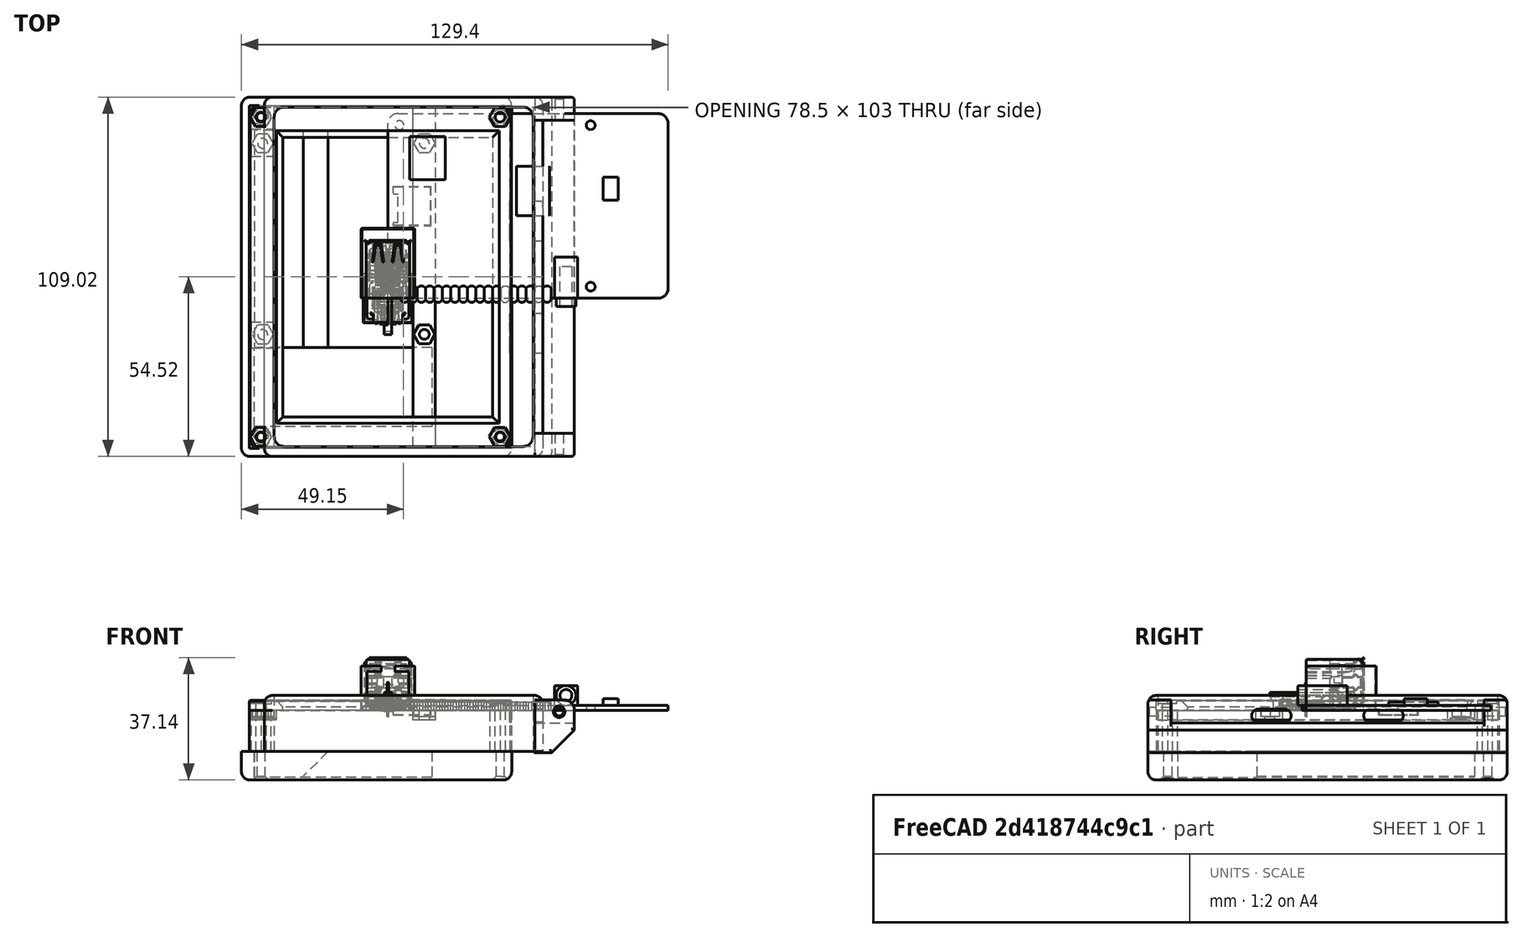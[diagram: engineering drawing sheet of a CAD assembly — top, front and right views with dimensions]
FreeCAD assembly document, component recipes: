
FREECAD ASSEMBLY — COMPONENT RECIPES ("computer-side")

This assembly document has 5 components, labeled P0..P4 below (a component is one placed body or linked part). 4 of them carry a construction recipe — the FreeCAD feature program that regenerates the part from scratch, quoted from this document or its linked companion documents; the rest are supplied as boundary geometry only. No exploded tour is included for this assembly.
COMPONENT P0 — recipe-attached ("epaper module tray", modeled in this document).
Construction recipe (the document's own serialized feature program — sketch geometry with constraints, then the solid features built on it; lengths are millimeters unless a unit is written):

FEATURE [Sketcher::SketchObject] Sketch002
  FullyConstrained = false
  MapMode = 5
  Support = -> [XY_Plane005]
  sketch-geometry (16):
    g0: LineSegment StartX=34 StartY=-45 StartZ=0 EndX=-38.5 EndY=-45 EndZ=0
    g1: LineSegment StartX=-41.5 StartY=-42 StartZ=0 EndX=-41.5 EndY=55 EndZ=0
    g2: LineSegment StartX=-38.5 StartY=58 StartZ=0 EndX=34 EndY=58 EndZ=0
    g3: LineSegment StartX=37 StartY=55 StartZ=0 EndX=37 EndY=-42 EndZ=0
    g4: LineSegment StartX=-42 StartY=58.5 StartZ=0 EndX=37.5 EndY=58.5 EndZ=0
    g5: LineSegment StartX=37.5 StartY=58.5 StartZ=0 EndX=37.5 EndY=-45.5 EndZ=0
    g6: LineSegment StartX=37.5 StartY=-45.5 StartZ=0 EndX=-42 EndY=-45.5 EndZ=0
    g7: LineSegment StartX=-42 StartY=-45.5 StartZ=0 EndX=-42 EndY=58.5 EndZ=0
    g8: Circle CenterX=-38.5 CenterY=55 CenterZ=0 NormalX=0 NormalY=0 NormalZ=1 AngleXU=0 Radius=1.5
    g9: Circle CenterX=34 CenterY=55 CenterZ=0 NormalX=0 NormalY=0 NormalZ=1 AngleXU=0 Radius=1.5
    g10: Circle CenterX=-38.5 CenterY=-42 CenterZ=0 NormalX=0 NormalY=0 NormalZ=1 AngleXU=0 Radius=1.5
    g11: Circle CenterX=34 CenterY=-42 CenterZ=0 NormalX=0 NormalY=0 NormalZ=1 AngleXU=0 Radius=1.5
    g12: ArcOfCircle CenterX=-38.5 CenterY=55 CenterZ=0 NormalX=0 NormalY=0 NormalZ=1 AngleXU=0 Radius=3 StartAngle=3.14159 EndAngle=7.85398
    g13: ArcOfCircle CenterX=34 CenterY=55 CenterZ=0 NormalX=0 NormalY=0 NormalZ=1 AngleXU=0 Radius=3 StartAngle=1.5708 EndAngle=6.28319
    g14: ArcOfCircle CenterX=34 CenterY=-42 CenterZ=0 NormalX=0 NormalY=0 NormalZ=1 AngleXU=0 Radius=3 StartAngle=0 EndAngle=4.71239
    g15: ArcOfCircle CenterX=-38.5 CenterY=-42 CenterZ=0 NormalX=0 NormalY=0 NormalZ=1 AngleXU=0 Radius=3 StartAngle=4.71239 EndAngle=9.42478
  constraints (32):
    c: Horizontal(g0)
    c: Horizontal(g2)
    c: Vertical(g1)
    c: Vertical(g3)
    c: Coincident(g4,g5)
    c: Coincident(g5,g6)
    c: Coincident(g6,g7)
    c: Coincident(g7,g4)
    c: Horizontal(g4)
    c: Horizontal(g6)
    c: Vertical(g5)
    c: Vertical(g7)
    c: Equal(g10,g11)
    c: Equal(g10,g8)
    c: Equal(g10,g9)
    c: Diameter(g10) = 3
    c: Coincident(g12,g8)
    c: Coincident(g13,g9)
    c: Coincident(g14,g11)
    c: Coincident(g15,g10)
    c: Equal(g12,g13)
    c: Equal(g12,g14)
    c: Equal(g12,g15)
    c: Diameter(g12) = 6
    c: Coincident(g13,g3)
    c: Coincident(g13,g2)
    c: Coincident(g12,g2)
    c: Coincident(g12,g1)
    c: Coincident(g1,g15)
    c: Coincident(g0,g15)
    c: Coincident(g14,g0)
    c: Coincident(g14,g3)
FEATURE [PartDesign::Pad] Pad002
  Direction = (0,0,1)
  Length = 12.5
  Length2 = 10
  Profile = -> Sketch002
  ReferenceAxis = -> Sketch002 [N_Axis]
  Reversed = true
  Type = 0
FEATURE [Sketcher::SketchObject] Sketch
  FullyConstrained = false
  MapMode = 5
  Support = -> [XY_Plane005]
  sketch-geometry (5):
    g0: LineSegment StartX=-33.867 StartY=51.1954 StartZ=0 EndX=-33.867 EndY=42.9605 EndZ=0
    g1: LineSegment StartX=-33.867 StartY=51.1954 StartZ=0 EndX=-41.8883 EndY=51.1954 EndZ=0
    g2: LineSegment StartX=-33.867 StartY=42.9605 StartZ=0 EndX=-41.8883 EndY=42.9605 EndZ=0
    g3: LineSegment StartX=-41.8883 StartY=51.1954 StartZ=0 EndX=-41.8883 EndY=42.9605 EndZ=0
    g4: Circle CenterX=-37.9976 CenterY=47.0105 CenterZ=0 NormalX=0 NormalY=0 NormalZ=1 AngleXU=0 Radius=1.5
  constraints (9):
    c: Vertical(g0)
    c: Coincident(g1,g0)
    c: Horizontal(g1)
    c: Coincident(g2,g0)
    c: Horizontal(g2)
    c: Coincident(g3,g1)
    c: Vertical(g3)
    c: Coincident(g3,g2)
    c: Diameter(g4) = 3
FEATURE [PartDesign::Pad] Pad
  BaseFeature = -> Pad002
  Direction = (0,0,1)
  Length = 2.5
  Length2 = 10
  Profile = -> Sketch
  ReferenceAxis = -> Sketch [N_Axis]
  Reversed = true
  Type = 0
FEATURE [Sketcher::SketchObject] Sketch032
  FullyConstrained = false
  MapMode = 5
  Support = -> [Pad]
  sketch-geometry (7):
    g0: LineSegment StartX=-34.726 StartY=46.9826 StartZ=0 EndX=-36.351 EndY=49.7971 EndZ=0
    g1: LineSegment StartX=-36.351 StartY=49.7971 StartZ=0 EndX=-39.601 EndY=49.7971 EndZ=0
    g2: LineSegment StartX=-39.601 StartY=49.7971 StartZ=0 EndX=-41.226 EndY=46.9826 EndZ=0
    g3: LineSegment StartX=-41.226 StartY=46.9826 StartZ=0 EndX=-39.601 EndY=44.168 EndZ=0
    g4: LineSegment StartX=-39.601 StartY=44.168 StartZ=0 EndX=-36.351 EndY=44.168 EndZ=0
    g5: LineSegment StartX=-36.351 StartY=44.168 StartZ=0 EndX=-34.726 EndY=46.9826 EndZ=0
    g6: Circle CenterX=-37.976 CenterY=46.9826 CenterZ=0 NormalX=0 NormalY=0 NormalZ=1 AngleXU=0 Radius=3.25
  constraints (15):
    c: Coincident(g0,g1)
    c: Coincident(g1,g2)
    c: Coincident(g2,g3)
    c: Coincident(g3,g4)
    c: Coincident(g4,g5)
    c: Coincident(g5,g0)
    c: Equal(g0, g1-g5) x5
    c: PointOnObject(g0,g6)
    c: PointOnObject(g1,g6)
    c: PointOnObject(g2,g6)
    c: PointOnObject(g3,g6)
    c: PointOnObject(g4,g6)
    c: PointOnObject(g5,g6)
    c: Diameter(g6) = 6.5
    c: Horizontal(g1)
FEATURE [PartDesign::Pocket] Pocket
  BaseFeature = -> Pad
  Direction = (0,0,-1)
  Length = 2
  Length2 = 5
  Profile = -> Sketch032
  ReferenceAxis = -> Sketch032 [N_Axis]
  Type = 0
FEATURE [Sketcher::SketchObject] Sketch033
  FullyConstrained = false
  MapMode = 5
  Support = -> [XY_Plane005]
  sketch-geometry (5):
    g0: LineSegment StartX=-41.8965 StartY=-7.25864 StartZ=0 EndX=-33.9497 EndY=-7.25864 EndZ=0
    g1: LineSegment StartX=-33.9497 StartY=-7.25864 StartZ=0 EndX=-33.9497 EndY=-15.2055 EndZ=0
    g2: LineSegment StartX=-33.9497 StartY=-15.2055 StartZ=0 EndX=-41.8965 EndY=-15.2055 EndZ=0
    g3: LineSegment StartX=-41.8965 StartY=-15.2055 StartZ=0 EndX=-41.8965 EndY=-7.25864 EndZ=0
    g4: Circle CenterX=-37.9911 CenterY=-11.0086 CenterZ=0 NormalX=0 NormalY=0 NormalZ=1 AngleXU=0 Radius=1.5
  constraints (9):
    c: Coincident(g0,g1)
    c: Coincident(g1,g2)
    c: Coincident(g2,g3)
    c: Coincident(g3,g0)
    c: Horizontal(g0)
    c: Horizontal(g2)
    c: Vertical(g1)
    c: Vertical(g3)
    c: Diameter(g4) = 3
FEATURE [PartDesign::Pad] Pad003
  BaseFeature = -> Pocket
  Direction = (0,0,1)
  Length = 3
  Length2 = 10
  Profile = -> Sketch033
  ReferenceAxis = -> Sketch033 [N_Axis]
  Reversed = true
  Type = 0
FEATURE [Sketcher::SketchObject] Sketch034
  FullyConstrained = false
  MapMode = 5
  Support = -> [XY_Plane005]
  sketch-geometry (6):
    g0: LineSegment StartX=7.58059 StartY=58.3477 StartZ=0 EndX=14.382 EndY=58.3477 EndZ=0
    g1: LineSegment StartX=14.382 StartY=58.3477 StartZ=0 EndX=14.382 EndY=-45.3233 EndZ=0
    g2: LineSegment StartX=14.382 StartY=-45.3233 StartZ=0 EndX=7.58059 EndY=-45.3233 EndZ=0
    g3: LineSegment StartX=7.58059 StartY=-45.3233 StartZ=0 EndX=7.58059 EndY=58.3477 EndZ=0
    g4: Circle CenterX=11.0339 CenterY=47.0265 CenterZ=0 NormalX=0 NormalY=0 NormalZ=1 AngleXU=0 Radius=1.5
    g5: Circle CenterX=11.0339 CenterY=-10.9673 CenterZ=0 NormalX=0 NormalY=0 NormalZ=1 AngleXU=0 Radius=1.5
  constraints (11):
    c: Coincident(g0,g1)
    c: Coincident(g1,g2)
    c: Coincident(g2,g3)
    c: Coincident(g3,g0)
    c: Horizontal(g0)
    c: Horizontal(g2)
    c: Vertical(g1)
    c: Vertical(g3)
    c: Equal(g5,g4)
    c: Diameter(g5) = 3
    c: Vertical(g4,g5)
FEATURE [PartDesign::Pad] Pad004
  BaseFeature = -> Pad003
  Direction = (0,0,1)
  Length = 3
  Length2 = 10
  Profile = -> Sketch034
  ReferenceAxis = -> Sketch034 [N_Axis]
  Reversed = true
  Type = 0
FEATURE [Sketcher::SketchObject] Sketch035
  FullyConstrained = false
  MapMode = 5
  Support = -> [Pad004]
  sketch-geometry (7):
    g0: LineSegment StartX=-36.3268 StartY=-8.14599 StartZ=0 EndX=-39.5768 EndY=-8.14599 EndZ=0
    g1: LineSegment StartX=-39.5768 StartY=-8.14599 StartZ=0 EndX=-41.2018 EndY=-10.9606 EndZ=0
    g2: LineSegment StartX=-41.2018 StartY=-10.9606 StartZ=0 EndX=-39.5768 EndY=-13.7752 EndZ=0
    g3: LineSegment StartX=-39.5768 StartY=-13.7752 StartZ=0 EndX=-36.3268 EndY=-13.7752 EndZ=0
    g4: LineSegment StartX=-36.3268 StartY=-13.7752 StartZ=0 EndX=-34.7018 EndY=-10.9606 EndZ=0
    g5: LineSegment StartX=-34.7018 StartY=-10.9606 StartZ=0 EndX=-36.3268 EndY=-8.14599 EndZ=0
    g6: Circle CenterX=-37.9518 CenterY=-10.9606 CenterZ=0 NormalX=0 NormalY=0 NormalZ=1 AngleXU=0 Radius=3.25
  constraints (15):
    c: Coincident(g0,g1)
    c: Coincident(g1,g2)
    c: Coincident(g2,g3)
    c: Coincident(g3,g4)
    c: Coincident(g4,g5)
    c: Coincident(g5,g0)
    c: Equal(g0, g1-g5) x5
    c: PointOnObject(g0,g6)
    c: PointOnObject(g1,g6)
    c: PointOnObject(g2,g6)
    c: PointOnObject(g3,g6)
    c: PointOnObject(g4,g6)
    c: PointOnObject(g5,g6)
    c: Horizontal(g0)
    c: Diameter(g6) = 6.5
FEATURE [PartDesign::Pocket] Pocket001
  BaseFeature = -> Pad004
  Direction = (0,0,-1)
  Length = 2
  Length2 = 5
  Profile = -> Sketch035
  ReferenceAxis = -> Sketch035 [N_Axis]
  Type = 0
FEATURE [Sketcher::SketchObject] Sketch036
  FullyConstrained = false
  MapMode = 5
  Support = -> [Pocket001]
  sketch-geometry (7):
    g0: LineSegment StartX=12.6781 StartY=49.8538 StartZ=0 EndX=9.42807 EndY=49.8538 EndZ=0
    g1: LineSegment StartX=9.42807 StartY=49.8538 StartZ=0 EndX=7.80307 EndY=47.0392 EndZ=0
    g2: LineSegment StartX=7.80307 StartY=47.0392 StartZ=0 EndX=9.42807 EndY=44.2246 EndZ=0
    g3: LineSegment StartX=9.42807 StartY=44.2246 StartZ=0 EndX=12.6781 EndY=44.2246 EndZ=0
    g4: LineSegment StartX=12.6781 StartY=44.2246 StartZ=0 EndX=14.3031 EndY=47.0392 EndZ=0
    g5: LineSegment StartX=14.3031 StartY=47.0392 StartZ=0 EndX=12.6781 EndY=49.8538 EndZ=0
    g6: Circle CenterX=11.0531 CenterY=47.0392 CenterZ=0 NormalX=0 NormalY=0 NormalZ=1 AngleXU=0 Radius=3.25
  constraints (15):
    c: Coincident(g0,g1)
    c: Coincident(g1,g2)
    c: Coincident(g2,g3)
    c: Coincident(g3,g4)
    c: Coincident(g4,g5)
    c: Coincident(g5,g0)
    c: Equal(g0, g1-g5) x5
    c: PointOnObject(g0,g6)
    c: PointOnObject(g1,g6)
    c: PointOnObject(g2,g6)
    c: PointOnObject(g3,g6)
    c: PointOnObject(g4,g6)
    c: PointOnObject(g5,g6)
    c: Diameter(g6) = 6.5
    c: Horizontal(g0)
FEATURE [PartDesign::Pocket] Pocket002
  BaseFeature = -> Pocket001
  Direction = (0,0,-1)
  Length = 2
  Length2 = 5
  Profile = -> Sketch036
  ReferenceAxis = -> Sketch036 [N_Axis]
  Type = 0
FEATURE [Sketcher::SketchObject] Sketch037
  FullyConstrained = false
  MapMode = 5
  Support = -> [Pocket002]
  sketch-geometry (7):
    g0: LineSegment StartX=12.6362 StartY=-8.1216 StartZ=0 EndX=9.3862 EndY=-8.1216 EndZ=0
    g1: LineSegment StartX=9.3862 StartY=-8.1216 StartZ=0 EndX=7.7612 EndY=-10.9362 EndZ=0
    g2: LineSegment StartX=7.7612 StartY=-10.9362 StartZ=0 EndX=9.3862 EndY=-13.7508 EndZ=0
    g3: LineSegment StartX=9.3862 StartY=-13.7508 StartZ=0 EndX=12.6362 EndY=-13.7508 EndZ=0
    g4: LineSegment StartX=12.6362 StartY=-13.7508 StartZ=0 EndX=14.2612 EndY=-10.9362 EndZ=0
    g5: LineSegment StartX=14.2612 StartY=-10.9362 StartZ=0 EndX=12.6362 EndY=-8.1216 EndZ=0
    g6: Circle CenterX=11.0112 CenterY=-10.9362 CenterZ=0 NormalX=0 NormalY=0 NormalZ=1 AngleXU=0 Radius=3.25
  constraints (15):
    c: Coincident(g0,g1)
    c: Coincident(g1,g2)
    c: Coincident(g2,g3)
    c: Coincident(g3,g4)
    c: Coincident(g4,g5)
    c: Coincident(g5,g0)
    c: Equal(g0, g1-g5) x5
    c: PointOnObject(g0,g6)
    c: PointOnObject(g1,g6)
    c: PointOnObject(g2,g6)
    c: PointOnObject(g3,g6)
    c: PointOnObject(g4,g6)
    c: PointOnObject(g5,g6)
    c: Diameter(g6) = 6.5
    c: Horizontal(g0)
FEATURE [PartDesign::Pocket] Pocket003
  BaseFeature = -> Pocket002
  Direction = (0,0,-1)
  Length = 2
  Length2 = 5
  Profile = -> Sketch037
  ReferenceAxis = -> Sketch037 [N_Axis]
  Type = 0
FEATURE [Sketcher::SketchObject] Sketch058
  AttachmentOffset = pos=(0,0,37) rot=(0,0,1;0rad)
  FullyConstrained = false
  MapMode = 5
  Placement = pos=(37,-8.2e-15,8.2e-15) rot=(0.57735,0.57735,0.57735;2.0944rad)
  Support = -> [YZ_Plane005]
  sketch-geometry (8):
    g0: ArcOfCircle CenterX=-14.544 CenterY=-1.63349 CenterZ=0 NormalX=0 NormalY=0 NormalZ=1 AngleXU=0 Radius=2 StartAngle=1.5708 EndAngle=4.71239
    g1: ArcOfCircle CenterX=-6.544 CenterY=-1.63349 CenterZ=0 NormalX=0 NormalY=0 NormalZ=1 AngleXU=0 Radius=2 StartAngle=4.71239 EndAngle=7.85398
    g2: LineSegment StartX=-14.544 StartY=-3.63349 StartZ=0 EndX=-6.54401 EndY=-3.63349 EndZ=0
    g3: LineSegment StartX=-6.54401 StartY=0.366508 StartZ=0 EndX=-14.544 EndY=0.366508 EndZ=0
    g4: ArcOfCircle CenterX=19.456 CenterY=-1.63349 CenterZ=0 NormalX=0 NormalY=0 NormalZ=1 AngleXU=0 Radius=2 StartAngle=1.5708 EndAngle=4.71239
    g5: ArcOfCircle CenterX=27.456 CenterY=-1.63349 CenterZ=0 NormalX=0 NormalY=0 NormalZ=1 AngleXU=0 Radius=2 StartAngle=4.71239 EndAngle=7.85398
    g6: LineSegment StartX=19.456 StartY=-3.63349 StartZ=0 EndX=27.456 EndY=-3.63349 EndZ=0
    g7: LineSegment StartX=27.456 StartY=0.366508 StartZ=0 EndX=19.456 EndY=0.366508 EndZ=0
  constraints (18):
    c: Tangent(g0,g2) = -1.5708
    c: Tangent(g2,g1) = -1.5708
    c: Tangent(g1,g3) = -1.5708
    c: Tangent(g3,g0) = -1.5708
    c: Equal(g0,g1)
    c: Tangent(g4,g6) = -1.5708
    c: Tangent(g6,g5) = -1.5708
    c: Tangent(g5,g7) = -1.5708
    c: Tangent(g7,g4) = -1.5708
    c: Equal(g4,g5)
    c: Horizontal(g3)
    c: Horizontal(g7)
    c: Equal(g3,g7)
    c: Equal(g1,g4)
    c: DistanceX(g1,g4) = 26
    c: DistanceY(g0,g0) = 4
    c: Horizontal(g1,g4)
    c: DistanceX(g0,g1) = 8
FEATURE [PartDesign::Pocket] Pocket027
  BaseFeature = -> Pocket003
  Direction = (-1,2e-16,-3e-16)
  Length = 0
  Length2 = 5
  Profile = -> Sketch058
  ReferenceAxis = -> Sketch058 [N_Axis]
  Reversed = true
  Type = 2
FEATURE [PartDesign::Body] Body002
  Group = -> [Sketch002,Pad002,Sketch,Pad,Sketch032,Pocket,Sketch033,Pad003,Sketch034,Pad004,Sketch035,Pocket001,Sketch036,Pocket002,Sketch037,Pocket003,Sketch058,Pocket027]
  Origin = -> Origin005
  Tip = -> Pocket027
COMPONENT P1 — recipe-attached ("epaper module cover", modeled in this document).
Construction recipe (the document's own serialized feature program — sketch geometry with constraints, then the solid features built on it; lengths are millimeters unless a unit is written):

FEATURE [PartDesign::Body] Body003  label="nuts"
  Origin = -> Origin007
FEATURE [Sketcher::SketchObject] Sketch003
  AttachmentOffset = pos=(0,0,2) rot=(0,0,1;0rad)
  FullyConstrained = false
  MapMode = 5
  Placement = pos=(0,0,2) rot=(0,0,1;0rad)
  Support = -> [XY_Plane008]
  sketch-geometry (7):
    g0: LineSegment StartX=-35.284 StartY=54.9433 StartZ=0 EndX=-36.909 EndY=57.7579 EndZ=0
    g1: LineSegment StartX=-36.909 StartY=57.7579 StartZ=0 EndX=-40.159 EndY=57.7579 EndZ=0
    g2: LineSegment StartX=-40.159 StartY=57.7579 StartZ=0 EndX=-41.784 EndY=54.9433 EndZ=0
    g3: LineSegment StartX=-41.784 StartY=54.9433 StartZ=0 EndX=-40.159 EndY=52.1287 EndZ=0
    g4: LineSegment StartX=-40.159 StartY=52.1287 StartZ=0 EndX=-36.909 EndY=52.1287 EndZ=0
    g5: LineSegment StartX=-36.909 StartY=52.1287 StartZ=0 EndX=-35.284 EndY=54.9433 EndZ=0
    g6: Circle CenterX=-38.534 CenterY=54.9433 CenterZ=0 NormalX=0 NormalY=0 NormalZ=1 AngleXU=0 Radius=3.25
  constraints (14):
    c: Coincident(g0,g1)
    c: Coincident(g1,g2)
    c: Coincident(g2,g3)
    c: Coincident(g3,g4)
    c: Coincident(g4,g5)
    c: Coincident(g5,g0)
    c: Equal(g0, g1-g5) x5
    c: PointOnObject(g0,g6)
    c: PointOnObject(g1,g6)
    c: PointOnObject(g2,g6)
    c: PointOnObject(g3,g6)
    c: PointOnObject(g4,g6)
    c: PointOnObject(g5,g6)
    c: Horizontal(g1)
FEATURE [Sketcher::SketchObject] Sketch005
  FullyConstrained = false
  MapMode = 5
  Support = -> [XY_Plane008]
  sketch-geometry (8):
    g0: LineSegment StartX=-42 StartY=58.5 StartZ=0 EndX=37.5 EndY=58.5 EndZ=0
    g1: LineSegment StartX=37.5 StartY=58.5 StartZ=0 EndX=37.5 EndY=-45.5 EndZ=0
    g2: LineSegment StartX=37.5 StartY=-45.5 StartZ=0 EndX=-42 EndY=-45.5 EndZ=0
    g3: LineSegment StartX=-42 StartY=-45.5 StartZ=0 EndX=-42 EndY=58.5 EndZ=0
    g4: LineSegment StartX=-31.8439 StartY=48.8107 StartZ=0 EndX=31.7561 EndY=48.8107 EndZ=0
    g5: LineSegment StartX=31.7561 StartY=48.8107 StartZ=0 EndX=31.7561 EndY=-35.9893 EndZ=0
    g6: LineSegment StartX=31.7561 StartY=-35.9893 StartZ=0 EndX=-31.8439 EndY=-35.9893 EndZ=0
    g7: LineSegment StartX=-31.8439 StartY=-35.9893 StartZ=0 EndX=-31.8439 EndY=48.8107 EndZ=0
  constraints (22):
    c: Coincident(g0,g1)
    c: Coincident(g1,g2)
    c: Coincident(g2,g3)
    c: Coincident(g3,g0)
    c: Horizontal(g0)
    c: Horizontal(g2)
    c: Vertical(g1)
    c: Vertical(g3)
    c: Coincident(g4,g5)
    c: Coincident(g5,g6)
    c: Coincident(g6,g7)
    c: Coincident(g7,g4)
    c: Horizontal(g4)
    c: Horizontal(g6)
    c: Vertical(g5)
    c: Vertical(g7)
    c: DistanceX(g4,g4) = 63.6
    c: DistanceY(g7,g7) = 84.8
    c: DistanceX(g0,g0) = 79.5
    c: DistanceY(g3,g3) = 104
    c: DistanceY(g1,g-1) = 45.5
    c: DistanceX(g-1,g1) = 37.5
FEATURE [PartDesign::Pad] Pad005
  Direction = (0,0,1)
  Length = 3
  Length2 = 10
  Profile = -> Sketch005
  ReferenceAxis = -> Sketch005 [N_Axis]
  Type = 0
FEATURE [PartDesign::Pocket] Pocket004
  BaseFeature = -> Pad005
  Direction = (0,0,-1)
  Length = 2
  Length2 = 5
  Profile = -> Sketch003
  ReferenceAxis = -> Sketch003 [N_Axis]
  Reversed = true
  Type = 0
FEATURE [Sketcher::SketchObject] Sketch006
  AttachmentOffset = pos=(0,0,2) rot=(0,0,1;0rad)
  FullyConstrained = false
  MapMode = 5
  Placement = pos=(0,0,2) rot=(0,0,1;0rad)
  Support = -> [XY_Plane008]
  sketch-geometry (7):
    g0: LineSegment StartX=-35.284 StartY=-42.0567 StartZ=0 EndX=-36.909 EndY=-39.2421 EndZ=0
    g1: LineSegment StartX=-36.909 StartY=-39.2421 StartZ=0 EndX=-40.159 EndY=-39.2421 EndZ=0
    g2: LineSegment StartX=-40.159 StartY=-39.2421 StartZ=0 EndX=-41.784 EndY=-42.0567 EndZ=0
    g3: LineSegment StartX=-41.784 StartY=-42.0567 StartZ=0 EndX=-40.159 EndY=-44.8713 EndZ=0
    g4: LineSegment StartX=-40.159 StartY=-44.8713 StartZ=0 EndX=-36.909 EndY=-44.8713 EndZ=0
    g5: LineSegment StartX=-36.909 StartY=-44.8713 StartZ=0 EndX=-35.284 EndY=-42.0567 EndZ=0
    g6: Circle CenterX=-38.534 CenterY=-42.0567 CenterZ=0 NormalX=0 NormalY=0 NormalZ=1 AngleXU=0 Radius=3.25
  constraints (14):
    c: Coincident(g0,g1)
    c: Coincident(g1,g2)
    c: Coincident(g2,g3)
    c: Coincident(g3,g4)
    c: Coincident(g4,g5)
    c: Coincident(g5,g0)
    c: Equal(g0, g1-g5) x5
    c: PointOnObject(g0,g6)
    c: PointOnObject(g1,g6)
    c: PointOnObject(g2,g6)
    c: PointOnObject(g3,g6)
    c: PointOnObject(g4,g6)
    c: PointOnObject(g5,g6)
    c: Horizontal(g1)
FEATURE [Sketcher::SketchObject] Sketch007
  AttachmentOffset = pos=(0,0,2) rot=(0,0,1;0rad)
  FullyConstrained = false
  MapMode = 5
  Placement = pos=(0,0,2) rot=(0,0,1;0rad)
  Support = -> [XY_Plane008]
  sketch-geometry (7):
    g0: LineSegment StartX=30.716 StartY=-42.0567 StartZ=0 EndX=32.341 EndY=-44.8713 EndZ=0
    g1: LineSegment StartX=32.341 StartY=-44.8713 StartZ=0 EndX=35.591 EndY=-44.8713 EndZ=0
    g2: LineSegment StartX=35.591 StartY=-44.8713 StartZ=0 EndX=37.216 EndY=-42.0567 EndZ=0
    g3: LineSegment StartX=37.216 StartY=-42.0567 StartZ=0 EndX=35.591 EndY=-39.2421 EndZ=0
    g4: LineSegment StartX=35.591 StartY=-39.2421 StartZ=0 EndX=32.341 EndY=-39.2421 EndZ=0
    g5: LineSegment StartX=32.341 StartY=-39.2421 StartZ=0 EndX=30.716 EndY=-42.0567 EndZ=0
    g6: Circle CenterX=33.966 CenterY=-42.0567 CenterZ=0 NormalX=0 NormalY=0 NormalZ=1 AngleXU=0 Radius=3.25
  constraints (15):
    c: Coincident(g0,g1)
    c: Coincident(g1,g2)
    c: Coincident(g2,g3)
    c: Coincident(g3,g4)
    c: Coincident(g4,g5)
    c: Coincident(g5,g0)
    c: Equal(g0, g1-g5) x5
    c: PointOnObject(g0,g6)
    c: PointOnObject(g1,g6)
    c: PointOnObject(g2,g6)
    c: PointOnObject(g3,g6)
    c: PointOnObject(g4,g6)
    c: PointOnObject(g5,g6)
    c: Horizontal(g4)
    c: Diameter(g6) = 6.5
FEATURE [PartDesign::Pocket] Pocket005
  BaseFeature = -> Pocket004
  Direction = (0,0,-1)
  Length = 2
  Length2 = 5
  Profile = -> Sketch007
  ReferenceAxis = -> Sketch007 [N_Axis]
  Reversed = true
  Type = 0
FEATURE [Sketcher::SketchObject] Sketch008
  AttachmentOffset = pos=(0,0,2) rot=(0,0,1;0rad)
  FullyConstrained = false
  MapMode = 5
  Placement = pos=(0,0,2) rot=(0,0,1;0rad)
  Support = -> [XY_Plane008]
  sketch-geometry (7):
    g0: LineSegment StartX=32.341 StartY=52.1287 StartZ=0 EndX=35.591 EndY=52.1287 EndZ=0
    g1: LineSegment StartX=35.591 StartY=52.1287 StartZ=0 EndX=37.216 EndY=54.9433 EndZ=0
    g2: LineSegment StartX=37.216 StartY=54.9433 StartZ=0 EndX=35.591 EndY=57.7579 EndZ=0
    g3: LineSegment StartX=35.591 StartY=57.7579 StartZ=0 EndX=32.341 EndY=57.7579 EndZ=0
    g4: LineSegment StartX=32.341 StartY=57.7579 StartZ=0 EndX=30.716 EndY=54.9433 EndZ=0
    g5: LineSegment StartX=30.716 StartY=54.9433 StartZ=0 EndX=32.341 EndY=52.1287 EndZ=0
    g6: Circle CenterX=33.966 CenterY=54.9433 CenterZ=0 NormalX=0 NormalY=0 NormalZ=1 AngleXU=0 Radius=3.25
  constraints (14):
    c: Coincident(g0,g1)
    c: Coincident(g1,g2)
    c: Coincident(g2,g3)
    c: Coincident(g3,g4)
    c: Coincident(g4,g5)
    c: Coincident(g5,g0)
    c: Equal(g0, g1-g5) x5
    c: PointOnObject(g0,g6)
    c: PointOnObject(g1,g6)
    c: PointOnObject(g2,g6)
    c: PointOnObject(g3,g6)
    c: PointOnObject(g4,g6)
    c: PointOnObject(g5,g6)
    c: Horizontal(g0)
FEATURE [PartDesign::Pocket] Pocket006
  BaseFeature = -> Pocket005
  Direction = (0,0,-1)
  Length = 2
  Length2 = 5
  Profile = -> Sketch008
  ReferenceAxis = -> Sketch008 [N_Axis]
  Reversed = true
  Type = 0
FEATURE [PartDesign::Pocket] Pocket007
  BaseFeature = -> Pocket006
  Direction = (0,0,-1)
  Length = 2
  Length2 = 5
  Profile = -> Sketch006
  ReferenceAxis = -> Sketch006 [N_Axis]
  Reversed = true
  Type = 0
FEATURE [Sketcher::SketchObject] Sketch009
  FullyConstrained = false
  MapMode = 5
  Support = -> [XY_Plane008]
  sketch-geometry (4):
    g0: Circle CenterX=-38.5151 CenterY=-42.0925 CenterZ=0 NormalX=0 NormalY=0 NormalZ=1 AngleXU=0 Radius=1.5
    g1: Circle CenterX=34.0278 CenterY=-42.0925 CenterZ=0 NormalX=0 NormalY=0 NormalZ=1 AngleXU=0 Radius=1.5
    g2: Circle CenterX=34.0278 CenterY=54.9676 CenterZ=0 NormalX=0 NormalY=0 NormalZ=1 AngleXU=0 Radius=1.5
    g3: Circle CenterX=-38.5151 CenterY=54.9676 CenterZ=0 NormalX=0 NormalY=0 NormalZ=1 AngleXU=0 Radius=1.5
  constraints (8):
    c: Equal(g3,g2)
    c: Equal(g3,g1)
    c: Equal(g3,g0)
    c: Diameter(g3) = 3
    c: Horizontal(g0,g1)
    c: Horizontal(g3,g2)
    c: Vertical(g3,g0)
    c: Vertical(g1,g2)
FEATURE [PartDesign::Pocket] Pocket008
  BaseFeature = -> Pocket007
  Direction = (0,0,-1)
  Length = 5
  Length2 = 5
  Midplane = true
  Profile = -> Sketch009
  ReferenceAxis = -> Sketch009 [N_Axis]
  Type = 1
FEATURE [PartDesign::Fillet] Fillet001
  Base = -> Pocket008 [Edge1,Edge5,Edge8,Edge2]
  BaseFeature = -> Pocket008
  Radius = 3
  SupportTransform = false
  UseAllEdges = false
FEATURE [PartDesign::Chamfer] Chamfer
  Angle = 45
  Base = -> Fillet001 [Edge44,Edge43,Edge42,Edge41]
  BaseFeature = -> Fillet001
  ChamferType = 0
  FlipDirection = false
  Size = 2
  Size2 = 1
  SupportTransform = false
  UseAllEdges = false
FEATURE [PartDesign::Chamfer] Chamfer009
  Angle = 45
  Base = -> Chamfer [Edge12,Edge10,Edge8,Edge11,Edge9,Edge7,Edge5,Edge6]
  BaseFeature = -> Chamfer
  ChamferType = 0
  FlipDirection = false
  Size = 0.2
  Size2 = 1
  SupportTransform = false
  UseAllEdges = false
FEATURE [PartDesign::Body] Body004  label="Body010"
  Group = -> [Sketch005,Pad005,Sketch003,Sketch008,Sketch006,Sketch007,Pocket004,Pocket005,Pocket006,Pocket007,Sketch009,Pocket008,Fillet001,Chamfer,Chamfer009]
  Origin = -> Origin008
  Tip = -> Chamfer009
COMPONENT P2 — recipe-attached ("outer-shell", modeled in this document).
Construction recipe (the document's own serialized feature program — sketch geometry with constraints, then the solid features built on it; lengths are millimeters unless a unit is written):

FEATURE [Sketcher::SketchObject] Sketch010
  FullyConstrained = true
  MapMode = 5
  Support = -> [XY_Plane010]
  sketch-geometry (8):
    g0: LineSegment StartX=-34.5 StartY=58 StartZ=0 EndX=44 EndY=58 EndZ=0
    g1: LineSegment StartX=44 StartY=58 StartZ=0 EndX=44 EndY=-45 EndZ=0
    g2: LineSegment StartX=44 StartY=-45 StartZ=0 EndX=-34.5 EndY=-45 EndZ=0
    g3: LineSegment StartX=-34.5 StartY=-45 StartZ=0 EndX=-34.5 EndY=58 EndZ=0
    g4: LineSegment StartX=-37.5 StartY=61 StartZ=0 EndX=47 EndY=61 EndZ=0
    g5: LineSegment StartX=47 StartY=61 StartZ=0 EndX=47 EndY=-48 EndZ=0
    g6: LineSegment StartX=47 StartY=-48 StartZ=0 EndX=-37.5 EndY=-48 EndZ=0
    g7: LineSegment StartX=-37.5 StartY=-48 StartZ=0 EndX=-37.5 EndY=61 EndZ=0
  constraints (24):
    c: Coincident(g0,g1)
    c: Coincident(g1,g2)
    c: Coincident(g2,g3)
    c: Coincident(g3,g0)
    c: Horizontal(g0)
    c: Horizontal(g2)
    c: Vertical(g1)
    c: Vertical(g3)
    c: Coincident(g4,g5)
    c: Coincident(g5,g6)
    c: Coincident(g6,g7)
    c: Coincident(g7,g4)
    c: Horizontal(g4)
    c: Horizontal(g6)
    c: Vertical(g5)
    c: Vertical(g7)
    c: DistanceX(g0,g0) = 78.5
    c: DistanceY(g3,g3) = 103
    c: DistanceY(g1,g-1) = 45
    c: DistanceX(g-1,g1) = 44
    c: DistanceY(g0,g4) = 3
    c: DistanceX(g4,g0) = 3
    c: DistanceX(g0,g4) = 3
    c: DistanceY(g5,g1) = 3
FEATURE [PartDesign::Pad] Pad006
  Direction = (0,0,1)
  Length = 17
  Length2 = 10
  Profile = -> Sketch010
  ReferenceAxis = -> Sketch010 [N_Axis]
  Reversed = true
  Type = 0
FEATURE [PartDesign::Fillet] Fillet
  Base = -> Pad006 [Edge13,Edge20,Edge14,Edge17]
  BaseFeature = -> Pad006
  Radius = 3
  SupportTransform = false
  UseAllEdges = false
FEATURE [PartDesign::Fillet] Fillet002
  Base = -> Fillet [Edge34,Edge33,Edge35,Edge36,Edge15,Edge14,Edge13,Edge12]
  BaseFeature = -> Fillet
  Radius = 2.5
  SupportTransform = false
  UseAllEdges = false
FEATURE [Sketcher::SketchObject] Sketch051
  AttachmentOffset = pos=(0,0,37) rot=(0,0,1;0rad)
  FullyConstrained = true
  MapMode = 5
  Placement = pos=(37,-8.2e-15,8.2e-15) rot=(0.57735,0.57735,0.57735;2.0944rad)
  Support = -> [YZ_Plane053]
  sketch-geometry (8):
    g0: LineSegment StartX=-48 StartY=6 StartZ=0 EndX=-41 EndY=6 EndZ=0
    g1: LineSegment StartX=-41 StartY=6 StartZ=0 EndX=-41 EndY=13 EndZ=0
    g2: LineSegment StartX=61 StartY=6 StartZ=0 EndX=54 EndY=6 EndZ=0
    g3: LineSegment StartX=54 StartY=6 StartZ=0 EndX=54 EndY=13 EndZ=0
    g4: LineSegment StartX=-48 StartY=22 StartZ=0 EndX=61 EndY=22 EndZ=0
    g5: LineSegment StartX=54 StartY=13 StartZ=0 EndX=-41 EndY=13 EndZ=0
    g6: LineSegment StartX=61 StartY=22 StartZ=0 EndX=61 EndY=6 EndZ=0
    g7: LineSegment StartX=-48 StartY=22 StartZ=0 EndX=-48 EndY=6 EndZ=0
  constraints (24):
    c: Coincident(g0,g1)
    c: Horizontal(g0)
    c: Vertical(g1)
    c: Coincident(g2,g3)
    c: Horizontal(g2)
    c: Vertical(g3)
    c: Horizontal(g4)
    c: Horizontal(g5)
    c: Coincident(g1,g5)
    c: Coincident(g5,g3)
    c: DistanceX(g4,g4) = 109
    c: Coincident(g6,g4)
    c: Coincident(g6,g2)
    c: Vertical(g6)
    c: Coincident(g7,g4)
    c: Coincident(g7,g0)
    c: Vertical(g7)
    c: Equal(g1,g3)
    c: Equal(g0,g2)
    c: DistanceX(g4,g-1) = 48
    c: DistanceY(g-1,g4) = 22
    c: DistanceX(g5,g5) = 95
    c: DistanceY(g6,g6) = 16
    c: DistanceY(g3,g3) = 7
FEATURE [PartDesign::Pad] Pad013
  Direction = (1,-2e-16,3e-16)
  Length = 12
  Length2 = 10
  Placement = pos=(0,0,0) rot=(0.57735,0.57735,0.57735;2.0944rad)
  Profile = -> Sketch051
  ReferenceAxis = -> Sketch051 [N_Axis]
  Type = 0
FEATURE [PartDesign::Chamfer] Chamfer013
  Angle = 45
  Base = -> Pad013 [Edge24]
  BaseFeature = -> Pad013
  ChamferType = 0
  FlipDirection = false
  Placement = pos=(0,0,0) rot=(0.57735,0.57735,0.57735;2.0944rad)
  Size = 6.9
  Size2 = 1
  SupportTransform = false
  UseAllEdges = false
FEATURE [PartDesign::Fillet] Fillet028  label="Fillet029"
  Base = -> Chamfer013 [Edge21]
  BaseFeature = -> Chamfer013
  Placement = pos=(0,0,0) rot=(0.57735,0.57735,0.57735;2.0944rad)
  Radius = 1
  SupportTransform = false
  UseAllEdges = false
FEATURE [PartDesign::Fillet] Fillet027  label="Fillet028"
  Base = -> Fillet028 [Edge4,Edge9]
  BaseFeature = -> Fillet028
  Placement = pos=(0,0,0) rot=(0.57735,0.57735,0.57735;2.0944rad)
  Radius = 3
  SupportTransform = false
  UseAllEdges = false
FEATURE [PartDesign::Fillet] Fillet029  label="Fillet030"
  Base = -> Fillet027 [Edge19,Edge16,Edge4,Edge18,Edge20]
  BaseFeature = -> Fillet027
  Placement = pos=(0,0,0) rot=(0.57735,0.57735,0.57735;2.0944rad)
  Radius = 1
  SupportTransform = false
  UseAllEdges = false
FEATURE [Sketcher::SketchObject] Sketch052
  FullyConstrained = true
  MapMode = 5
  Placement = pos=(2.68e-14,61,-1.34e-14) rot=(0.57735,0.57735,0.57735;4.18879rad)
  Support = -> [Fillet029]
  sketch-geometry (1):
    g0: Circle CenterX=9.54001 CenterY=44.3562 CenterZ=0 NormalX=0 NormalY=0 NormalZ=1 AngleXU=0 Radius=1.25
  constraints (2):
    c: Diameter(g0) = 2.5
    c: Block(g0)
FEATURE [PartDesign::Pocket] Pocket020
  BaseFeature = -> Fillet029
  Direction = (-4e-16,-1,2e-16)
  Length = 5
  Length2 = 5
  Placement = pos=(0,0,0) rot=(0.57735,0.57735,0.57735;2.0944rad)
  Profile = -> Sketch052
  ReferenceAxis = -> Sketch052 [N_Axis]
  Type = 1
FEATURE [PartDesign::Chamfer] Chamfer014
  Angle = 45
  Base = -> Pocket020 [Edge46,Edge29]
  BaseFeature = -> Pocket020
  ChamferType = 0
  FlipDirection = false
  Placement = pos=(0,0,0) rot=(0.57735,0.57735,0.57735;2.0944rad)
  Size = 0.5
  Size2 = 1
  SupportTransform = false
  UseAllEdges = false
FEATURE [PartDesign::Fillet] Fillet031  label="Fillet032"
  Base = -> Chamfer014 [Edge5,Edge3,Edge2,Edge4,Edge6]
  BaseFeature = -> Chamfer014
  Placement = pos=(0,0,0) rot=(0.57735,0.57735,0.57735;2.0944rad)
  Radius = 1
  SupportTransform = false
  UseAllEdges = false
FEATURE [PartDesign::Body] Body012  label="left"
  Group = -> [Sketch051,Pad013,Chamfer013,Fillet028,Fillet027,Fillet029,Sketch052,Pocket020,Chamfer014,Fillet031]
  Origin = -> Origin053
  Placement = pos=(7.57,12.98,9.09) rot=(1,0,0;3.14159rad)
  Tip = -> Fillet031
FEATURE [Sketcher::SketchObject] Sketch053
  FullyConstrained = false
  MapMode = 5
  Placement = pos=(47,0,0) rot=(0.57735,0.57735,0.57735;2.0944rad)
  Support = -> [Fillet002]
  sketch-geometry (8):
    g0: ArcOfCircle CenterX=-14.5432 CenterY=-6.15181 CenterZ=0 NormalX=0 NormalY=0 NormalZ=1 AngleXU=0 Radius=2 StartAngle=1.5708 EndAngle=4.71239
    g1: ArcOfCircle CenterX=-6.54324 CenterY=-6.15181 CenterZ=0 NormalX=0 NormalY=0 NormalZ=1 AngleXU=0 Radius=2 StartAngle=4.71239 EndAngle=7.85398
    g2: LineSegment StartX=-14.5432 StartY=-8.15181 StartZ=0 EndX=-6.54324 EndY=-8.15181 EndZ=0
    g3: LineSegment StartX=-6.54324 StartY=-4.15181 StartZ=0 EndX=-14.5432 EndY=-4.15181 EndZ=0
    g4: ArcOfCircle CenterX=19.4568 CenterY=-6.15181 CenterZ=0 NormalX=0 NormalY=0 NormalZ=1 AngleXU=0 Radius=2 StartAngle=1.5708 EndAngle=4.71239
    g5: ArcOfCircle CenterX=27.4568 CenterY=-6.15181 CenterZ=0 NormalX=0 NormalY=0 NormalZ=1 AngleXU=0 Radius=2 StartAngle=4.71239 EndAngle=7.85398
    g6: LineSegment StartX=19.4568 StartY=-8.15181 StartZ=0 EndX=27.4568 EndY=-8.15181 EndZ=0
    g7: LineSegment StartX=27.4568 StartY=-4.15181 StartZ=0 EndX=19.4568 EndY=-4.15181 EndZ=0
  constraints (18):
    c: Tangent(g0,g2) = -1.5708
    c: Tangent(g2,g1) = -1.5708
    c: Tangent(g1,g3) = -1.5708
    c: Tangent(g3,g0) = -1.5708
    c: Equal(g0,g1)
    c: Horizontal(g2)
    c: Tangent(g4,g6) = -1.5708
    c: Tangent(g6,g5) = -1.5708
    c: Tangent(g5,g7) = -1.5708
    c: Tangent(g7,g4) = -1.5708
    c: Equal(g4,g5)
    c: Horizontal(g6)
    c: Equal(g3,g7)
    c: Equal(g1,g4)
    c: DistanceY(g1,g1) = 4
    c: Horizontal(g1,g4)
    c: DistanceX(g0,g1) = 8
    c: DistanceX(g1,g4) = 26
FEATURE [PartDesign::Pocket] Pocket021
  BaseFeature = -> Fillet002
  Direction = (-1,0,0)
  Length = 11
  Length2 = 5
  Profile = -> Sketch053
  ReferenceAxis = -> Sketch053 [N_Axis]
  Type = 2
FEATURE [PartDesign::Body] Body005  label="Body011"
  Group = -> [Sketch010,Pad006,Fillet,Fillet002,Sketch053,Pocket021]
  Origin = -> Origin010
  Placement = pos=(0,0,4.5) rot=(0,0,1;0rad)
  Tip = -> Pocket021
COMPONENT P3 — geometry summary ("PCBA: Raspberry Pi 4B"; no construction recipe available for this part):
  bounding box: 90.1 x 58.5 x 19.0 mm
  tessellated surface: 40,066 triangles
  volume: 18599 mm^3 (19% of its bounding box)
COMPONENT P4 — recipe-attached ("proto-rear-cover", modeled in this document).
Construction recipe (the document's own serialized feature program — sketch geometry with constraints, then the solid features built on it; lengths are millimeters unless a unit is written):

FEATURE [Sketcher::SketchObject] Sketch059
  AttachmentOffset = pos=(0,0,-61) rot=(0,0,1;0rad)
  FullyConstrained = false
  MapMode = 5
  Placement = pos=(0,61,1.35e-14) rot=(1,0,0;1.5708rad)
  Support = -> [XZ_Plane055]
  sketch-geometry (4):
    g0: LineSegment StartX=-44.4037 StartY=-12.5015 StartZ=0 EndX=37.5266 EndY=-12.5015 EndZ=0
    g1: LineSegment StartX=37.5266 StartY=-12.5015 StartZ=0 EndX=37.5266 EndY=-21.1381 EndZ=0
    g2: LineSegment StartX=37.5266 StartY=-21.1381 StartZ=0 EndX=-44.4037 EndY=-21.1381 EndZ=0
    g3: LineSegment StartX=-44.4037 StartY=-21.1381 StartZ=0 EndX=-44.4037 EndY=-12.5015 EndZ=0
  constraints (8):
    c: Coincident(g0,g1)
    c: Coincident(g1,g2)
    c: Coincident(g2,g3)
    c: Coincident(g3,g0)
    c: Horizontal(g0)
    c: Horizontal(g2)
    c: Vertical(g1)
    c: Vertical(g3)
FEATURE [PartDesign::Pad] Pad014
  Direction = (0,-1,2e-16)
  Length = 109
  Length2 = 10
  Placement = pos=(0,0,0) rot=(1,0,0;1.5708rad)
  Profile = -> Sketch059
  ReferenceAxis = -> Sketch059 [N_Axis]
  Type = 0
FEATURE [PartDesign::Fillet] Fillet032  label="Fillet033"
  Base = -> Pad014 [Edge11,Edge6,Edge9,Edge8,Edge5,Edge7,Edge10,Edge12]
  BaseFeature = -> Pad014
  Placement = pos=(0,0,0) rot=(1,0,0;1.5708rad)
  Radius = 2.5
  SupportTransform = false
  UseAllEdges = false
FEATURE [Sketcher::SketchObject] Sketch060
  AttachmentOffset = pos=(0,0,39) rot=(0,0,1;0rad)
  FullyConstrained = false
  MapMode = 5
  Placement = pos=(0,-39,-8.7e-15) rot=(1,0,0;1.5708rad)
  Support = -> [XZ_Plane055]
  sketch-geometry (4):
    g0: LineSegment StartX=13.3456 StartY=-20.3299 StartZ=0 EndX=-40.4767 EndY=-20.3299 EndZ=0
    g1: LineSegment StartX=-40.4767 StartY=-20.3299 StartZ=0 EndX=-40.4767 EndY=-1.29457 EndZ=0
    g2: LineSegment StartX=-40.4767 StartY=-1.29457 StartZ=0 EndX=13.3456 EndY=-1.29457 EndZ=0
    g3: LineSegment StartX=13.3456 StartY=-1.29457 StartZ=0 EndX=13.3456 EndY=-20.3299 EndZ=0
  constraints (8):
    c: Coincident(g0,g1)
    c: Coincident(g1,g2)
    c: Coincident(g2,g3)
    c: Coincident(g3,g0)
    c: Horizontal(g0)
    c: Horizontal(g2)
    c: Vertical(g1)
    c: Vertical(g3)
FEATURE [PartDesign::Pocket] Pocket028
  BaseFeature = -> Fillet032
  Direction = (0,1,-2e-16)
  Length = 24
  Length2 = 5
  Placement = pos=(0,0,0) rot=(1,0,0;1.5708rad)
  Profile = -> Sketch060
  ReferenceAxis = -> Sketch060 [N_Axis]
  Type = 0
FEATURE [Sketcher::SketchObject] Sketch061
  AttachmentOffset = pos=(0,0,15) rot=(0,0,1;0rad)
  FullyConstrained = false
  MapMode = 5
  Placement = pos=(0,-15,-3.3e-15) rot=(1,0,0;1.5708rad)
  Support = -> [XZ_Plane055]
  sketch-geometry (4):
    g0: LineSegment StartX=-40.468 StartY=-20.2949 StartZ=0 EndX=-25.6424 EndY=-20.2949 EndZ=0
    g1: LineSegment StartX=-25.6424 StartY=-20.2949 StartZ=0 EndX=-25.6424 EndY=-11.2092 EndZ=0
    g2: LineSegment StartX=-25.6424 StartY=-11.2092 StartZ=0 EndX=-40.468 EndY=-11.2092 EndZ=0
    g3: LineSegment StartX=-40.468 StartY=-11.2092 StartZ=0 EndX=-40.468 EndY=-20.2949 EndZ=0
  constraints (8):
    c: Coincident(g0,g1)
    c: Coincident(g1,g2)
    c: Coincident(g2,g3)
    c: Coincident(g3,g0)
    c: Horizontal(g0)
    c: Horizontal(g2)
    c: Vertical(g1)
    c: Vertical(g3)
FEATURE [PartDesign::Pocket] Pocket029
  BaseFeature = -> Pocket028
  Direction = (0,1,-2e-16)
  Length = 66
  Length2 = 5
  Placement = pos=(0,0,0) rot=(1,0,0;1.5708rad)
  Profile = -> Sketch061
  ReferenceAxis = -> Sketch061 [N_Axis]
  Type = 0
FEATURE [PartDesign::Chamfer] Chamfer015
  Angle = 45
  Base = -> Pocket029 [Edge11]
  BaseFeature = -> Pocket029
  ChamferType = 0
  FlipDirection = false
  Placement = pos=(0,0,0) rot=(1,0,0;1.5708rad)
  Size = 7.5
  Size2 = 1
  SupportTransform = false
  UseAllEdges = false
FEATURE [Sketcher::SketchObject] Sketch062
  FullyConstrained = true
  MapMode = 5
  Placement = pos=(0,-1.4e-14,-21.1381) rot=(1,0,0;3.14159rad)
  Support = -> [Chamfer015]
  sketch-geometry (4):
    g0: Circle CenterX=-38.52 CenterY=42.0371 CenterZ=0 NormalX=0 NormalY=0 NormalZ=1 AngleXU=0 Radius=1.3
    g1: Circle CenterX=34.0083 CenterY=42.0371 CenterZ=0 NormalX=0 NormalY=0 NormalZ=1 AngleXU=0 Radius=1.3
    g2: Circle CenterX=34.0083 CenterY=-54.9772 CenterZ=0 NormalX=0 NormalY=0 NormalZ=1 AngleXU=0 Radius=1.3
    g3: Circle CenterX=-38.52 CenterY=-54.9772 CenterZ=0 NormalX=0 NormalY=0 NormalZ=1 AngleXU=0 Radius=1.3
  constraints (11):
    c: Equal(g3,g2)
    c: Equal(g3,g1)
    c: Equal(g3,g0)
    c: Diameter(g3) = 2.6
    c: Horizontal(g0,g1)
    c: Horizontal(g3,g2)
    c: Vertical(g3,g0)
    c: Vertical(g1,g2)
    c: Block(g0)
    c: Block(g3)
    c: Block(g2)
FEATURE [PartDesign::Pocket] Pocket030
  BaseFeature = -> Chamfer015
  Direction = (0,2e-16,1)
  Length = 5
  Length2 = 5
  Placement = pos=(0,0,0) rot=(1,0,0;1.5708rad)
  Profile = -> Sketch062
  ReferenceAxis = -> Sketch062 [N_Axis]
  Type = 1
FEATURE [PartDesign::Chamfer] Chamfer016
  Angle = 45
  Base = -> Pocket030 [Edge59,Edge65,Edge62,Edge38]
  BaseFeature = -> Pocket030
  ChamferType = 0
  FlipDirection = false
  Placement = pos=(0,0,0) rot=(1,0,0;1.5708rad)
  Size = 1
  Size2 = 1
  SupportTransform = false
  UseAllEdges = false
FEATURE [PartDesign::Body] Body
  Group = -> [Sketch059,Pad014,Fillet032,Sketch060,Pocket028,Sketch061,Pocket029,Chamfer015,Sketch062,Pocket030,Chamfer016]
  Origin = -> Origin055
  Tip = -> Chamfer016
PROVENANCE & LICENSES
A FreeCAD (.FCStd) document from a public repository crawl; recipes are the document's own serialized feature recipes (and, for linked parts, companion documents' recipes).
License: as declared in the source repository (recorded in the dataset sidecar).
